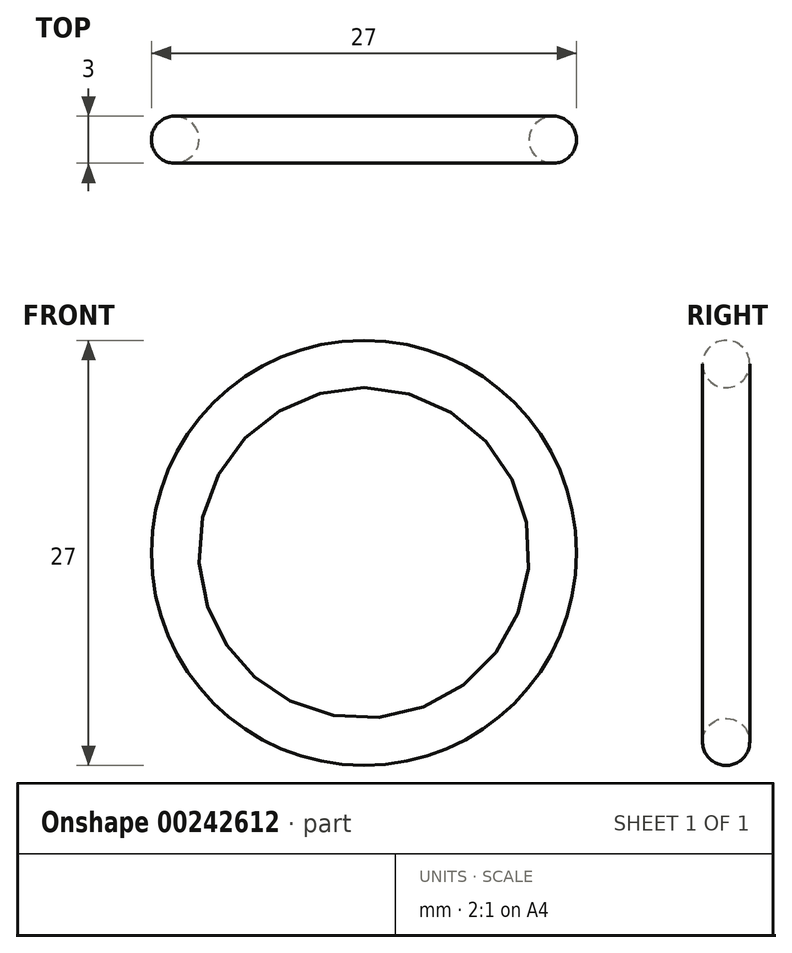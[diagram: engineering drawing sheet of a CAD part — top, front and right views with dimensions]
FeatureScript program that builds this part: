
annotation { "Feature Type Name" : "Feature", "Feature Type Description" : "" }
export const myFeature = defineFeature(function(context is Context, id is Id, definition is map)
    precondition{}
    {
        {
            var Q0;
            Q0=qCreatedBy(makeId("Front.planeOp"),FACE);
            var sketch = newSketch(context, id + "F0", { "sketchPlane" : qUnion([Q0])});
            skCircle(sketch, "E0", {"center": v(0, 0) * mm, "radius": 12 * mm});
            skSolve(sketch);
        }
        {
            var Q0;
            Q0=qCreatedBy(makeId("Right.planeOp"),FACE);
            var sketch = newSketch(context, id + "F1", { "sketchPlane" : qUnion([Q0])});
            skPoint(sketch, "E1", {"position": v(0, 12) * mm});
            skCircle(sketch, "E2", {"center": v(0, 12) * mm, "radius": 1.5 * mm});
            skSolve(sketch);
        }
        {
            var Q0;
            Q0=makeQuery(id+"F1.imprint","IMPRINT",FACE,{"disambiguationData":[TD([[makeQuery(id+"F1.imprint","IMPRINT",EDGE,{"derivedFrom":sQuery(id+"F1.wireOp",EDGE,"E2")}),1.0]])]});
            var Q1;
            Q1=sQuery(id+"F0.wireOp",EDGE,"E0");
            revolve(context, id + "F2", {"surfaceOperationType" : NewSurfaceOperationType.NEW, "entities" : qUnion([Q0]), "axis" : qUnion([Q1]), "revolveType" : RevolveType.FULL});
        }
    });
